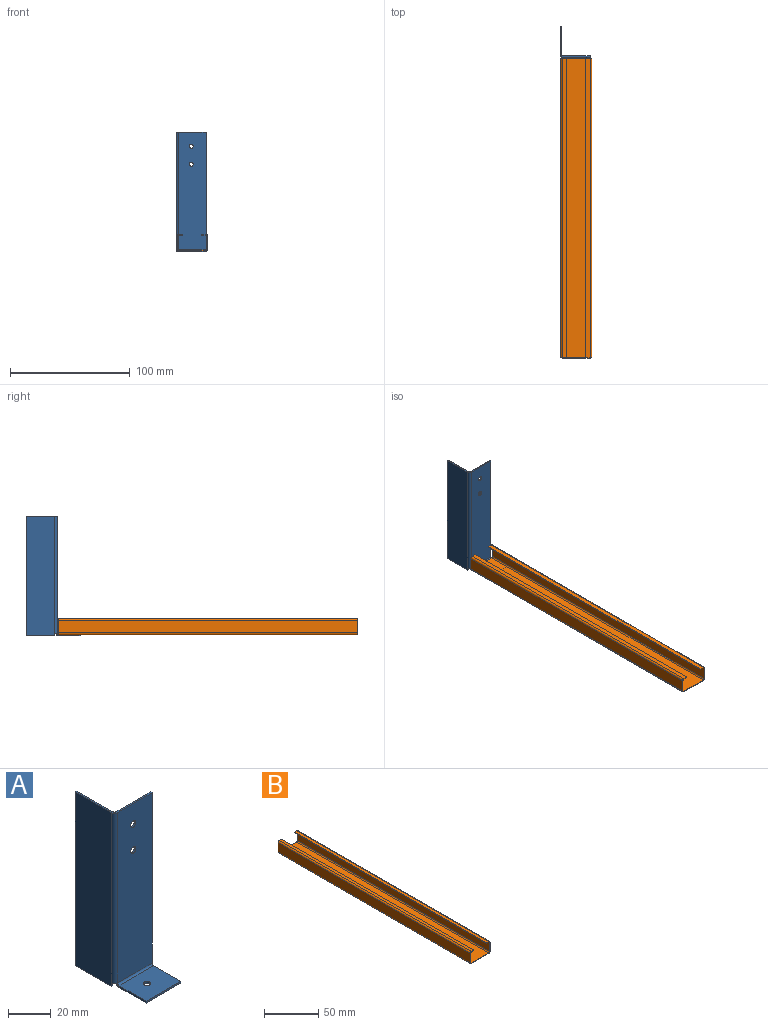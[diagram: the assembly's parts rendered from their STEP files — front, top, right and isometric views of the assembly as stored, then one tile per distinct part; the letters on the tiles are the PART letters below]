
ASSEMBLY  parts=2 mates=1
PART A: 26 faces, bbox 25x45x100 mm
  f0: plane 2x1mm, normal (0,-1,0), area 2mm2, adj f1,f4,f5,f22
  f1: plane 24x1mm, normal (0,0,-1), area 24mm2, adj f0,f3,f4,f5
  f2: plane 24x1mm, normal (0,0,1), area 24mm2, adj f3,f4,f5,f23
  f3: plane 100x1mm, normal (0,1,0), area 100mm2, adj f1,f2,f4,f5
  f4: plane 100x24mm, normal (-1,0,0), area 2400mm2, adj f0,f1,f2,f3,f24
  f5: plane 100x24mm, normal (1,0,0), area 2400mm2, adj f0,f1,f2,f3,f25
  f6: plane 98x1mm, normal (1,0,0), area 98mm2, adj f7,f10,f11,f19
  f7: plane 23x1mm, normal (0,0,1), area 23mm2, adj f6,f10,f11,f23
  f8: cylinder r=1.75mm len=3.5mm, axis (0,-1,0), area 11mm2, adj f10,f11
  f9: cylinder r=1.75mm len=3.5mm, axis (0,-1,0), area 11mm2, adj f10,f11
  f10: plane 98x23mm, normal (0,-1,0), area 2234.8mm2, adj f6,f7,f8,f9,f21,f24
  f11: plane 98x23mm, normal (0,1,0), area 2234.8mm2, adj f6,f7,f8,f9,f20,f25
  f12: plane 23x1mm, normal (0,-1,0), area 23mm2, adj f13,f15,f16,f17
  f13: plane 18x1mm, normal (1,0,0), area 18mm2, adj f12,f16,f17,f19
  f14: cylinder r=1.75mm len=3.5mm, axis (0,0,1), area 11mm2, adj f16,f17
  f15: plane 18x1mm, normal (-1,0,0), area 18mm2, adj f12,f16,f17,f18
  f16: plane 23x18mm, normal (0,0,1), area 404.4mm2, adj f12,f13,f14,f15,f21
  f17: plane 23x18mm, normal (0,0,-1), area 404.4mm2, adj f12,f13,f14,f15,f20
  f18: plane 2x2mm, normal (-1,0,0), area 2.4mm2, adj f15,f20,f21,f22
  f19: plane 2x2mm, normal (1,0,0), area 2.4mm2, adj f6,f13,f20,f21
  f20: cylinder r=2mm len=23mm, axis (-1,0,0), area 72.3mm2, adj f11,f17,f18,f19
  f21: cylinder r=1mm len=23mm, axis (-1,0,0), area 36.1mm2, adj f10,f16,f18,f19
  f22: plane 2x2mm, normal (0,0,-1), area 2.4mm2, adj f0,f18,f24,f25
  f23: plane 2x2mm, normal (0,0,1), area 2.4mm2, adj f2,f7,f24,f25
  f24: cylinder r=2mm len=98mm, axis (0,0,-1), area 307.9mm2, adj f4,f10,f22,f23
  f25: cylinder r=1mm len=98mm, axis (0,0,-1), area 153.9mm2, adj f5,f11,f22,f23
PART B: 38 faces, bbox 26x250x13.5 mm
  f0: plane 23x0.5mm, normal (0,-1,0), area 11.5mm2, adj f2,f3,f17,f34
  f1: plane 23x0.5mm, normal (0,1,0), area 11.5mm2, adj f2,f3,f18,f35
  f2: plane 250x23mm, normal (0,0,-1), area 5750mm2, adj f0,f1,f19,f36
  f3: plane 250x23mm, normal (0,0,1), area 5750mm2, adj f0,f1,f20,f37
  f4: plane 10.5x0.5mm, normal (0,1,0), area 5.2mm2, adj f6,f7,f14,f18
  f5: plane 10.5x0.5mm, normal (0,-1,0), area 5.2mm2, adj f6,f7,f13,f17
  f6: plane 250x10.5mm, normal (-1,0,0), area 2625mm2, adj f4,f5,f15,f19
  f7: plane 250x10.5mm, normal (1,0,0), area 2625mm2, adj f4,f5,f16,f20
  f8: plane 250x0.5mm, normal (1,0,0), area 125mm2, adj f9,f10,f11,f12
  f9: plane 3.5x0.5mm, normal (0,1,0), area 1.8mm2, adj f8,f11,f12,f14
  f10: plane 3.5x0.5mm, normal (0,-1,0), area 1.8mm2, adj f8,f11,f12,f13
  f11: plane 250x3.5mm, normal (0,0,1), area 875mm2, adj f8,f9,f10,f15
  f12: plane 250x3.5mm, normal (0,0,-1), area 875mm2, adj f8,f9,f10,f16
  f13: plane 1.5x1.5mm, normal (0,-1,0), area 1mm2, adj f5,f10,f15,f16
  f14: plane 1.5x1.5mm, normal (0,1,0), area 1mm2, adj f4,f9,f15,f16
  f15: cylinder r=1.5mm len=250mm, axis (0,-1,0), area 589mm2, adj f6,f11,f13,f14
  f16: cylinder r=1mm len=250mm, axis (0,-1,0), area 392.7mm2, adj f7,f12,f13,f14
  f17: plane 1.5x1.5mm, normal (0,-1,0), area 1mm2, adj f0,f5,f19,f20
  f18: plane 1.5x1.5mm, normal (0,1,0), area 1mm2, adj f1,f4,f19,f20
  f19: cylinder r=1.5mm len=250mm, axis (0,-1,0), area 589mm2, adj f2,f6,f17,f18
  f20: cylinder r=1mm len=250mm, axis (0,-1,0), area 392.7mm2, adj f3,f7,f17,f18
  f21: plane 10.5x0.5mm, normal (0,-1,0), area 5.2mm2, adj f23,f24,f31,f34
  f22: plane 10.5x0.5mm, normal (0,1,0), area 5.2mm2, adj f23,f24,f30,f35
  f23: plane 250x10.5mm, normal (1,0,0), area 2625mm2, adj f21,f22,f32,f36
  f24: plane 250x10.5mm, normal (-1,0,0), area 2625mm2, adj f21,f22,f33,f37
  f25: plane 250x0.5mm, normal (-1,0,0), area 125mm2, adj f26,f27,f28,f29
  f26: plane 3.5x0.5mm, normal (0,-1,0), area 1.8mm2, adj f25,f28,f29,f31
  f27: plane 3.5x0.5mm, normal (0,1,0), area 1.8mm2, adj f25,f28,f29,f30
  f28: plane 250x3.5mm, normal (0,0,1), area 875mm2, adj f25,f26,f27,f32
  f29: plane 250x3.5mm, normal (0,0,-1), area 875mm2, adj f25,f26,f27,f33
  f30: plane 1.5x1.5mm, normal (0,1,0), area 1mm2, adj f22,f27,f32,f33
  f31: plane 1.5x1.5mm, normal (0,-1,0), area 1mm2, adj f21,f26,f32,f33
  f32: cylinder r=1.5mm len=250mm, axis (0,1,0), area 589mm2, adj f23,f28,f30,f31
  f33: cylinder r=1mm len=250mm, axis (0,1,0), area 392.7mm2, adj f24,f29,f30,f31
  f34: plane 1.5x1.5mm, normal (0,-1,0), area 1mm2, adj f0,f21,f36,f37
  f35: plane 1.5x1.5mm, normal (0,1,0), area 1mm2, adj f1,f22,f36,f37
  f36: cylinder r=1.5mm len=250mm, axis (0,-1,0), area 589mm2, adj f2,f23,f34,f35
  f37: cylinder r=1mm len=250mm, axis (0,-1,0), area 392.7mm2, adj f3,f24,f34,f35
PLACE A rot(axis=(0.12,-0.92,-0.39),0deg) t=(-77.22,-151.09,-48.61)mm fixed
PLACE B rot(axis=(0.21,-0.92,-0.34),0deg) t=(-76.22,-156.95,-65.61)mm
MATE fastened A.f16 <-> B.f2  axis (0,0,1) through (-63.72,-156.95,-65.61)mm
